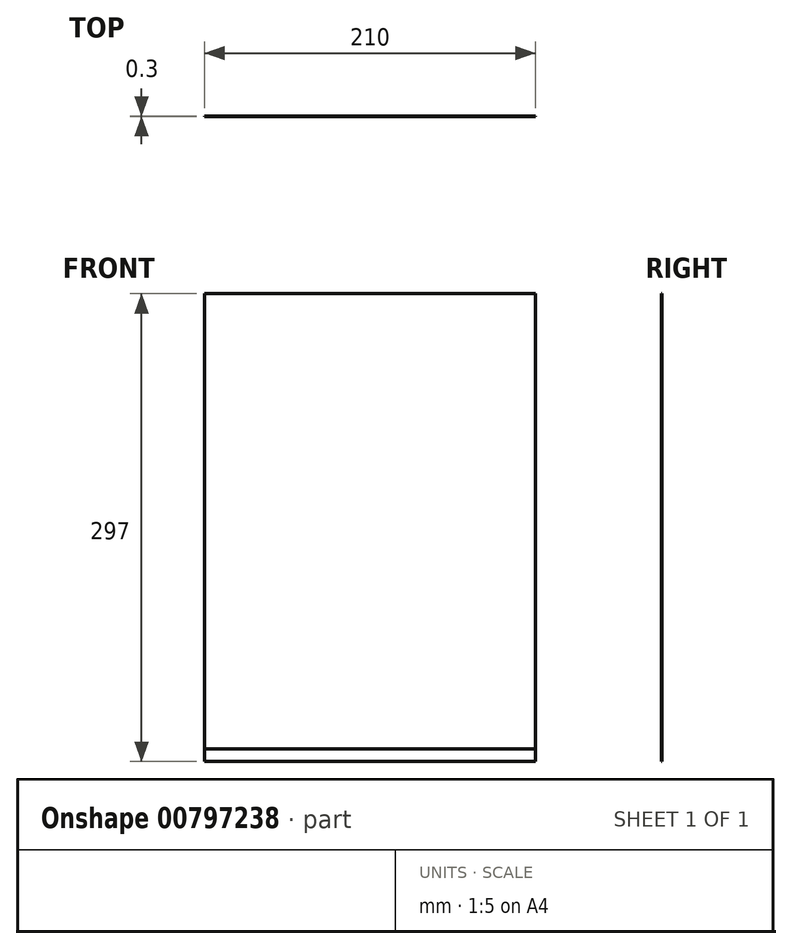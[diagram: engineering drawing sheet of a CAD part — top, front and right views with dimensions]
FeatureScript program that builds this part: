
annotation { "Feature Type Name" : "Feature", "Feature Type Description" : "" }
export const myFeature = defineFeature(function(context is Context, id is Id, definition is map)
    precondition{}
    {
        {
            var Q0;
            Q0=qCreatedBy(makeId("Front.planeOp"),FACE);
            var sketch = newSketch(context, id + "F0", { "sketchPlane" : qUnion([Q0])});
            skLineSegment(sketch, "E0.bottom", {"start": v(0, 0) * mm, "end": v(210, 0) * mm});
            skLineSegment(sketch, "E0.top", {"start": v(0, -297) * mm, "end": v(210, -297) * mm});
            skLineSegment(sketch, "E0.left", {"start": v(0, 0) * mm, "end": v(0, -297) * mm});
            skLineSegment(sketch, "E0.right", {"start": v(210, 0) * mm, "end": v(210, -297) * mm});
            skSolve(sketch);
        }
        {
            var Q0;
            Q0=makeQuery(id+"F0.imprint","IMPRINT",FACE,{"disambiguationData":[TD([[makeQuery(id+"F0.imprint","IMPRINT",EDGE,{"derivedFrom":sQuery(id+"F0.wireOp",EDGE,"E0.bottom")}),-1.0]])]});
            extrude(context, id + "F1", {"entities" : qUnion([Q0]), "depth" : 0.3 * mm, "offsetDistance" : 25 * mm});
        }
        {
            var Q0;
            Q0=makeQuery(id+"F1.opExtrude","CAP_FACE",FACE,{"disambiguationData":[OSD([sQuery(id+"F0.wireOp",EDGE,"E0.bottom"),sQuery(id+"F0.wireOp",EDGE,"E0.top"),sQuery(id+"F0.wireOp",EDGE,"E0.left"),sQuery(id+"F0.wireOp",EDGE,"E0.right")])],"isStart":true});
            var sketch = newSketch(context, id + "F2", { "sketchPlane" : qUnion([Q0])});
            skLineSegment(sketch, "E1.bottom", {"start": v(0, 0) * mm, "end": v(-210, 0) * mm});
            skLineSegment(sketch, "E1.top", {"start": v(0, -72.25) * mm, "end": v(-210, -72.25) * mm});
            skLineSegment(sketch, "E1.left", {"start": v(0, 0) * mm, "end": v(0, -72.25) * mm});
            skLineSegment(sketch, "E1.right", {"start": v(-210, 0) * mm, "end": v(-210, -72.25) * mm});
            skLineSegment(sketch, "E2.top", {"start": v(0, -144.5) * mm, "end": v(-210, -144.5) * mm});
            skLineSegment(sketch, "E2.left", {"start": v(0, -72.25) * mm, "end": v(0, -144.5) * mm});
            skLineSegment(sketch, "E2.right", {"start": v(-210, -72.25) * mm, "end": v(-210, -144.5) * mm});
            skLineSegment(sketch, "E3.top", {"start": v(0, -216.75) * mm, "end": v(-210, -216.75) * mm});
            skLineSegment(sketch, "E3.left", {"start": v(0, -144.5) * mm, "end": v(0, -216.75) * mm});
            skLineSegment(sketch, "E3.right", {"start": v(-210, -144.5) * mm, "end": v(-210, -216.75) * mm});
            skLineSegment(sketch, "E4.top", {"start": v(0, -289) * mm, "end": v(-210, -289) * mm});
            skLineSegment(sketch, "E4.left", {"start": v(0, -216.75) * mm, "end": v(0, -289) * mm});
            skLineSegment(sketch, "E4.right", {"start": v(-210, -216.75) * mm, "end": v(-210, -289) * mm});
            skSolve(sketch);
        }
        {
            var Q0;
            Q0=makeQuery(id+"F2.imprint","IMPRINT",FACE,{"disambiguationData":[TD([[makeQuery(id+"F2.imprint","IMPRINT",EDGE,{"derivedFrom":sQuery(id+"F2.wireOp",EDGE,"E1.bottom")}),1.0]])]});
            var Q1;
            Q1=makeQuery(id+"F2.imprint","IMPRINT",FACE,{"disambiguationData":[TD([[makeQuery(id+"F2.imprint","IMPRINT",EDGE,{"derivedFrom":sQuery(id+"F2.wireOp",EDGE,"E1.top")}),1.0]])]});
            var Q2;
            Q2=makeQuery(id+"F2.imprint","IMPRINT",FACE,{"disambiguationData":[TD([[makeQuery(id+"F2.imprint","IMPRINT",EDGE,{"derivedFrom":sQuery(id+"F2.wireOp",EDGE,"E2.top")}),1.0]])]});
            var Q3;
            Q3=makeQuery(id+"F2.imprint","IMPRINT",FACE,{"disambiguationData":[TD([[makeQuery(id+"F2.imprint","IMPRINT",EDGE,{"derivedFrom":sQuery(id+"F2.wireOp",EDGE,"E3.top")}),1.0]])]});
            extrude(context, id + "F3", {"entities" : qUnion([Q0, Q1, Q2, Q3]), "oppositeDirection" : true, "depth" : 0.3 * mm, "offsetDistance" : 25 * mm});
        }
    });
